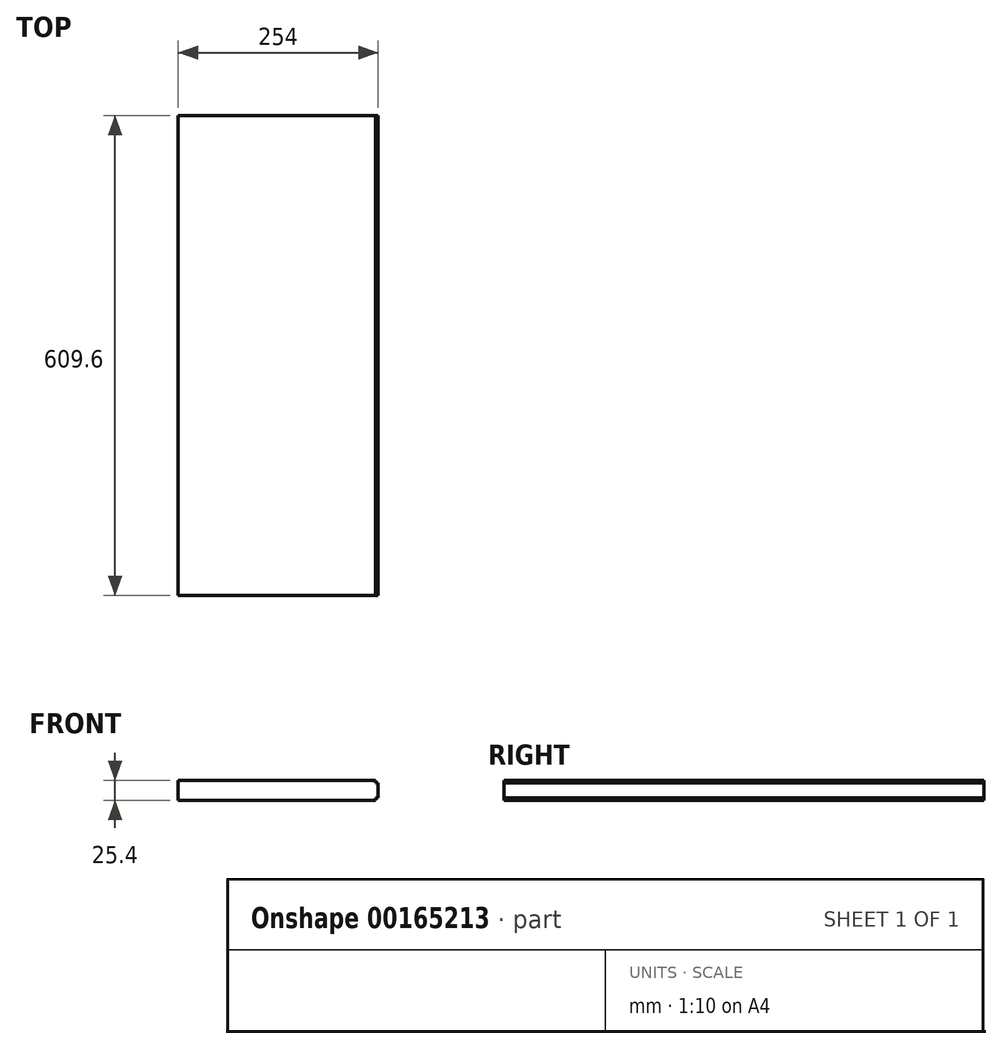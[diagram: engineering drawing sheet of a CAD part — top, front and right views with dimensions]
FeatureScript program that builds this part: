
annotation { "Feature Type Name" : "Feature", "Feature Type Description" : "" }
export const myFeature = defineFeature(function(context is Context, id is Id, definition is map)
    precondition{}
    {
        {
            var Q0;
            Q0=qCreatedBy(makeId("Top.planeOp"),FACE);
            var sketch = newSketch(context, id + "F0", { "sketchPlane" : qUnion([Q0])});
            skLineSegment(sketch, "E0.bottom", {"start": v(0, 0) * mm, "end": v(254, 0) * mm});
            skLineSegment(sketch, "E0.top", {"start": v(0, -609.6) * mm, "end": v(254, -609.6) * mm});
            skLineSegment(sketch, "E0.left", {"start": v(0, 0) * mm, "end": v(0, -609.6) * mm});
            skLineSegment(sketch, "E0.right", {"start": v(254, 0) * mm, "end": v(254, -609.6) * mm});
            skSolve(sketch);
        }
        {
            var Q0;
            Q0 = qSketchRegion(id + "F0", true);
            extrude(context, id + "F1", {"entities" : qUnion([Q0]), "depth" : 25.4 * mm});
        }
        {
            var Q0;
            Q0=makeQuery(id+"F1.opExtrude","SWEPT_FACE",FACE,{"disambiguationData":[OSD([sQuery(id+"F0.wireOp",EDGE,"E0.top")])]});
            var sketch = newSketch(context, id + "F2", { "sketchPlane" : qUnion([Q0])});
            skLineSegment(sketch, "E1.bottom", {"start": v(254, 25.4) * mm, "end": v(250.83, 25.4) * mm});
            skLineSegment(sketch, "E1.top", {"start": v(254, 22.22) * mm, "end": v(250.83, 22.22) * mm});
            skLineSegment(sketch, "E1.left", {"start": v(254, 25.4) * mm, "end": v(254, 22.22) * mm});
            skLineSegment(sketch, "E1.right", {"start": v(250.83, 25.4) * mm, "end": v(250.83, 22.23) * mm});
            skLineSegment(sketch, "E2.bottom", {"start": v(254, 0) * mm, "end": v(250.83, 0) * mm});
            skLineSegment(sketch, "E2.top", {"start": v(254, 3.17) * mm, "end": v(250.83, 3.17) * mm});
            skLineSegment(sketch, "E2.left", {"start": v(254, 0) * mm, "end": v(254, 3.17) * mm});
            skLineSegment(sketch, "E2.right", {"start": v(250.83, 0) * mm, "end": v(250.83, 3.17) * mm});
            skSolve(sketch);
        }
        {
            var Q0;
            Q0 = qSketchRegion(id + "F2", true);
            var Q1;
            Q1=makeQuery(id+"F1.opExtrude","SWEPT_FACE",FACE,{"disambiguationData":[OSD([sQuery(id+"F0.wireOp",EDGE,"E0.bottom")])]});
            extrude(context, id + "F3", {"entities" : qUnion([Q0]), "operationType" : NewBodyOperationType.REMOVE, "endBound" : BoundingType.UP_TO_SURFACE, "oppositeDirection" : true, "endBoundEntityFace" : qUnion([Q1]), "depth" : 25.4 * mm});
        }
    });
